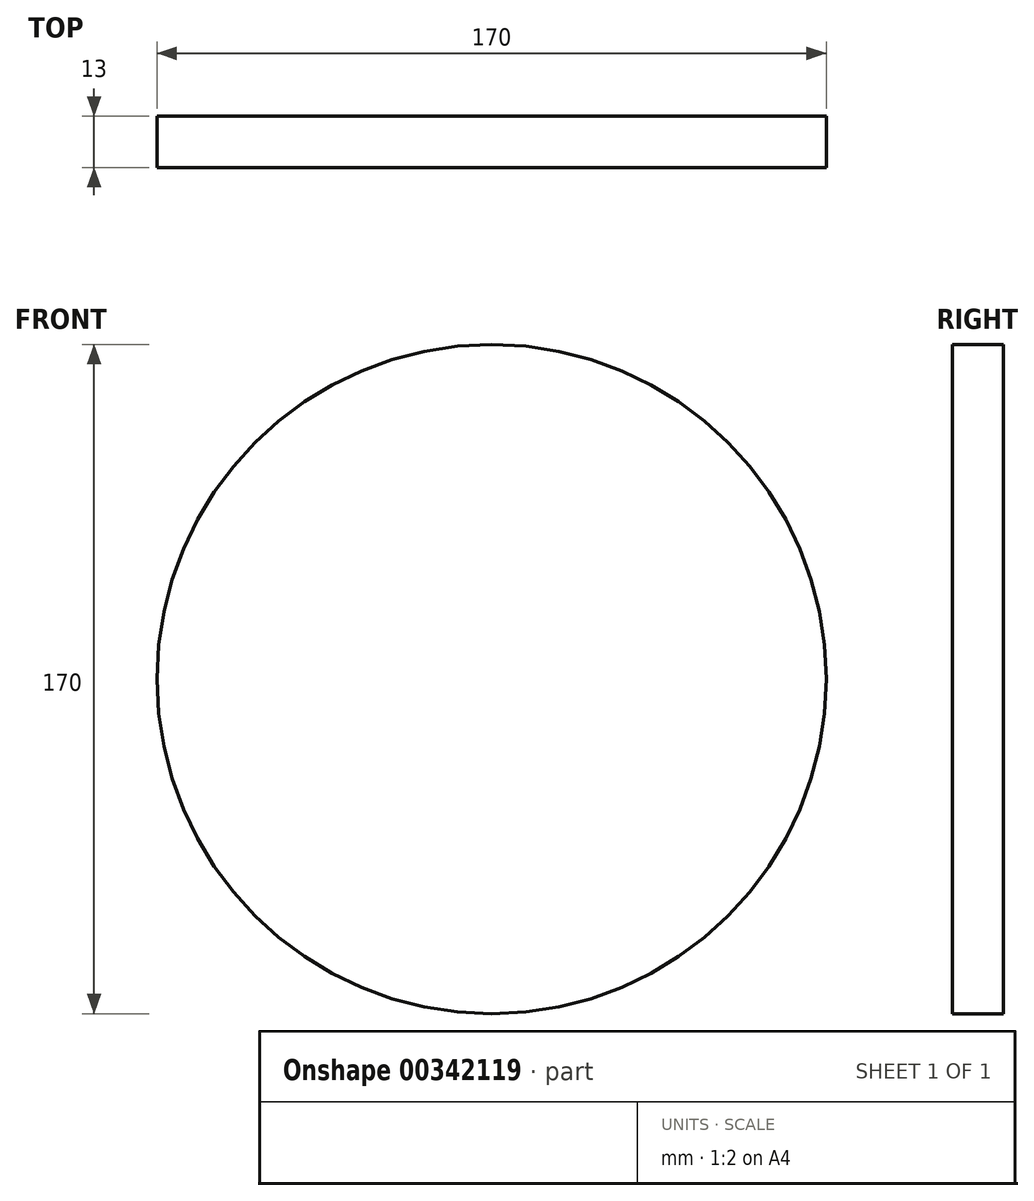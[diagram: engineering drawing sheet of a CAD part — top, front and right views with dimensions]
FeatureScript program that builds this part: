
annotation { "Feature Type Name" : "Feature", "Feature Type Description" : "" }
export const myFeature = defineFeature(function(context is Context, id is Id, definition is map)
    precondition{}
    {
        {
            var Q0;
            Q0=qCreatedBy(makeId("Front.planeOp"),FACE);
            var sketch = newSketch(context, id + "F0", { "sketchPlane" : qUnion([Q0])});
            skCircle(sketch, "E0", {"center": v(0, 0) * mm, "radius": 85 * mm});
            skSolve(sketch);
        }
        {
            var Q0;
            Q0=makeQuery(id+"F0.imprint","IMPRINT",FACE,{"disambiguationData":[TD([[makeQuery(id+"F0.imprint","IMPRINT",EDGE,{"derivedFrom":sQuery(id+"F0.wireOp",EDGE,"E0")}),1.0]])]});
            extrude(context, id + "F1", {"entities" : qUnion([Q0]), "depth" : 13 * mm});
        }
    });
